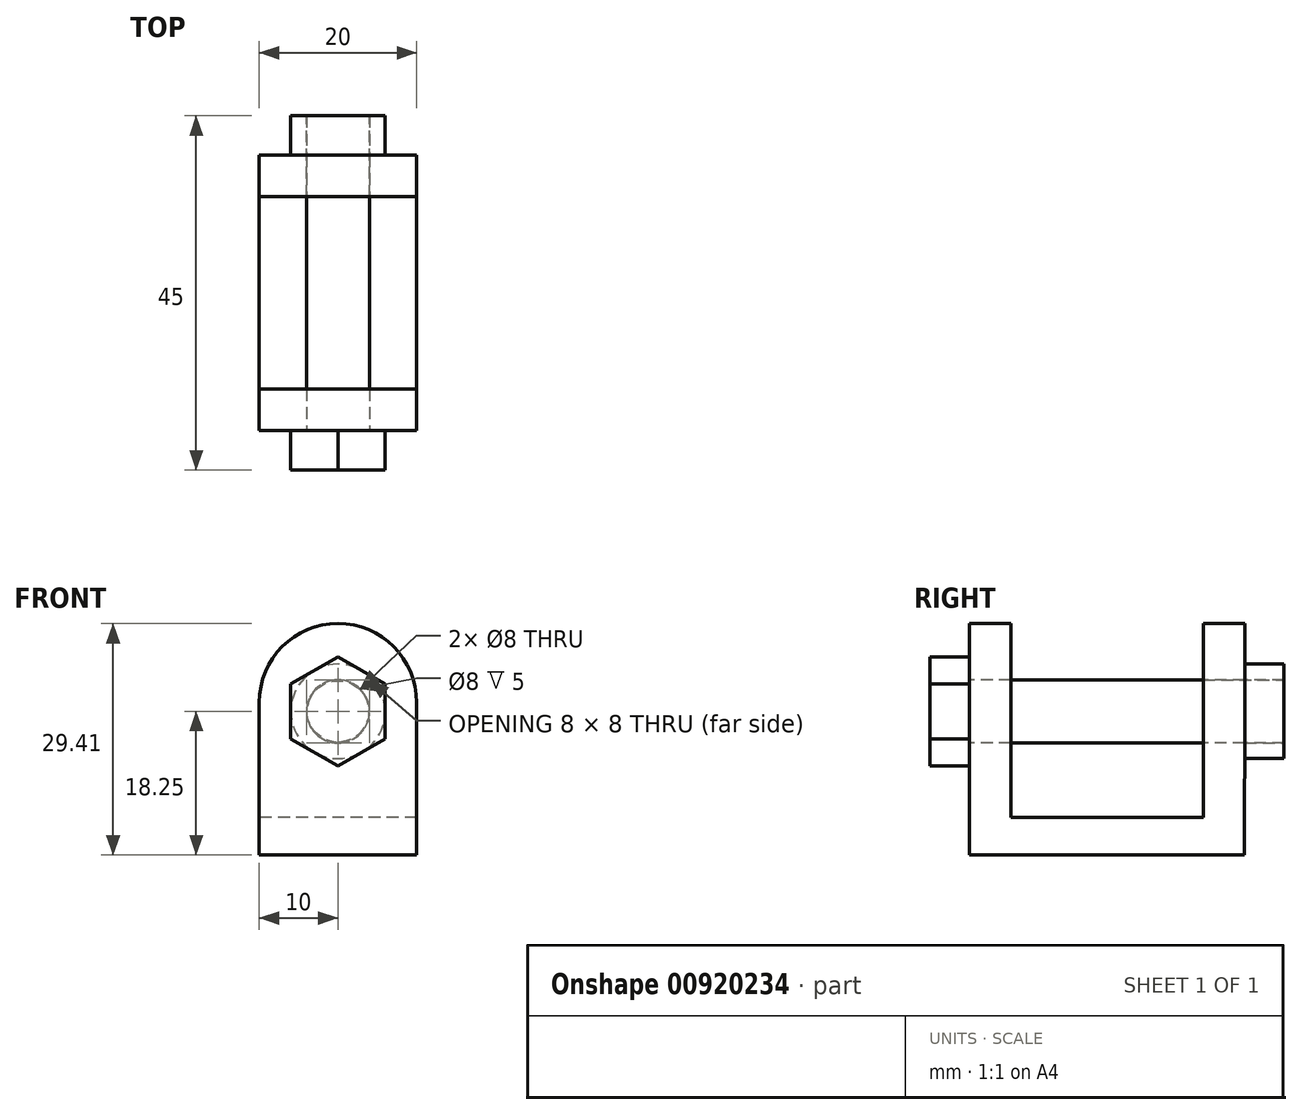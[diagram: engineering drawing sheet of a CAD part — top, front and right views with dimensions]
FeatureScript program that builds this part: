
annotation { "Feature Type Name" : "Feature", "Feature Type Description" : "" }
export const myFeature = defineFeature(function(context is Context, id is Id, definition is map)
    precondition{}
    {
        {
            var Q0;
            Q0=qCreatedBy(makeId("Front.planeOp"),FACE);
            var sketch = newSketch(context, id + "F0", { "sketchPlane" : qUnion([Q0])});
            skCircle(sketch, "E0", {"center": v(0, 0) * mm, "radius": 4 * mm});
            skSolve(sketch);
        }
        {
            var Q0;
            Q0 = qSketchRegion(id + "F0", true);
            extrude(context, id + "F1", {"entities" : qUnion([Q0]), "depth" : 40 * mm, "offsetDistance" : 25 * mm});
        }
        {
            var Q0;
            Q0=makeQuery(id+"F1.opExtrude","CAP_FACE",FACE,{"disambiguationData":[OSD([sQuery(id+"F0.wireOp",EDGE,"E0")])],"isStart":false});
            var sketch = newSketch(context, id + "F2", { "sketchPlane" : qUnion([Q0])});
            skCircle(sketch, "E1.cCircle", {"center": v(0, 0) * mm, "radius": 6 * mm, "construction": true});
            skLineSegment(sketch, "E1.0", {"start": v(6, 3.46) * mm, "end": v(6, -3.46) * mm});
            skLineSegment(sketch, "E1.1", {"start": v(6, -3.46) * mm, "end": v(0, -6.93) * mm});
            skLineSegment(sketch, "E1.2", {"start": v(0, -6.93) * mm, "end": v(-6, -3.46) * mm});
            skLineSegment(sketch, "E1.3", {"start": v(-6, -3.46) * mm, "end": v(-6, 3.46) * mm});
            skLineSegment(sketch, "E1.4", {"start": v(-6, 3.46) * mm, "end": v(0, 6.93) * mm});
            skLineSegment(sketch, "E1.5", {"start": v(0, 6.93) * mm, "end": v(6, 3.46) * mm});
            skPoint(sketch, "E1.0.midPoint", {"position": v(6, 0) * mm});
            skSolve(sketch);
        }
        {
            var Q0;
            Q0 = qSketchRegion(id + "F2", true);
            extrude(context, id + "F3", {"entities" : qUnion([Q0]), "operationType" : NewBodyOperationType.ADD, "depth" : 5 * mm, "offsetDistance" : 25 * mm});
        }
        {
            var Q0;
            Q0=makeQuery(id+"F1.opExtrude","CAP_FACE",FACE,{"disambiguationData":[OSD([sQuery(id+"F0.wireOp",EDGE,"E0")])],"isStart":true});
            var sketch = newSketch(context, id + "F4", { "sketchPlane" : qUnion([Q0])});
            skCircle(sketch, "E2", {"center": v(0, 0) * mm, "radius": 4 * mm});
            skCircle(sketch, "E3", {"center": v(0, 0) * mm, "radius": 6 * mm});
            skSolve(sketch);
        }
        {
            var Q0;
            Q0 = qSketchRegion(id + "F4", true);
            var Q1;
            Q1=makeQuery(id+"F4.imprint","IMPRINT",FACE,{"disambiguationData":[TD([[makeQuery(id+"F4.imprint","IMPRINT",EDGE,{"derivedFrom":sQuery(id+"F4.wireOp",EDGE,"E2")}),1.0]])]});
            extrude(context, id + "F5", {"entities" : qUnion([Q0, Q1]), "depth" : -5 * mm, "offsetDistance" : 25 * mm, "hasDraft" : true, "draftAngle" : 0 * degree});
        }
        {
            var Q0;
            Q0=qCreatedBy(makeId("Right.planeOp"),FACE);
            var sketch = newSketch(context, id + "F6", { "sketchPlane" : qUnion([Q0])});
            skLineSegment(sketch, "E4.top", {"start": v(-40, -18.25) * mm, "end": v(-5.02, -18.25) * mm});
            skLineSegment(sketch, "E5", {"start": v(-40, 11.16) * mm, "end": v(-40, -18.25) * mm});
            skLineSegment(sketch, "E6", {"start": v(-4.99, 11.16) * mm, "end": v(-5.02, -18.25) * mm});
            skLineSegment(sketch, "E7.right", {"start": v(-34.71, 0.02) * mm, "end": v(-34.71, 11.16) * mm});
            skLineSegment(sketch, "E8.right", {"start": v(-10.27, 0.02) * mm, "end": v(-10.27, 11.16) * mm});
            skLineSegment(sketch, "E9.top", {"start": v(-10.27, -13.48) * mm, "end": v(-34.71, -13.48) * mm});
            skLineSegment(sketch, "E9.left", {"start": v(-10.27, 0.02) * mm, "end": v(-10.27, -13.48) * mm});
            skLineSegment(sketch, "E9.right", {"start": v(-34.71, 0.02) * mm, "end": v(-34.71, -13.48) * mm});
            skLineSegment(sketch, "E10", {"start": v(-4.99, 11.16) * mm, "end": v(-10.27, 11.16) * mm});
            skLineSegment(sketch, "E11", {"start": v(-34.71, 11.16) * mm, "end": v(-40, 11.16) * mm});
            skSolve(sketch);
        }
        {
            var Q0;
            Q0 = qSketchRegion(id + "F6", true);
            extrude(context, id + "F7", {"entities" : qUnion([Q0]), "depth" : 10 * mm, "offsetDistance" : 25 * mm, "hasSecondDirection" : true, "secondDirectionOppositeDirection" : true, "secondDirectionDepth" : 10 * mm});
        }
        {
            var Q0;
            Q0=makeQuery(id+"F7.opExtrude","SWEPT_FACE",FACE,{"disambiguationData":[OSD([sQuery(id+"F6.wireOp",EDGE,"E5")])]});
            var sketch = newSketch(context, id + "F8", { "sketchPlane" : qUnion([Q0])});
            skPoint(sketch, "E12.orphan", {"position": v(10, 0) * mm});
            skPoint(sketch, "E13.top.start.orphan", {"position": v(-10, 0) * mm});
            skLineSegment(sketch, "E14.bottom", {"start": v(0, 11.16) * mm, "end": v(0, 11.16) * mm});
            skLineSegment(sketch, "E14.top", {"start": v(-10, 0) * mm, "end": v(10, 0) * mm});
            skLineSegment(sketch, "E14.left", {"start": v(-10, 1.16) * mm, "end": v(-10, 0) * mm});
            skLineSegment(sketch, "E14.right", {"start": v(10, 1.16) * mm, "end": v(10, 0) * mm});
            skPoint(sketch, "E15.visualSharp", {"position": v(-10, 11.16) * mm});
            skArc(sketch, "E15.filletArc", {"start": v(0, 11.16) * mm, "mid": v(-7.07, 8.24) * mm, "end": v(-10, 1.16) * mm});
            skPoint(sketch, "E16.visualSharp", {"position": v(10, 11.16) * mm});
            skArc(sketch, "E16.filletArc", {"start": v(10, 1.16) * mm, "mid": v(7.07, 8.24) * mm, "end": v(0, 11.16) * mm});
            skSolve(sketch);
        }
        {
            var Q0;
            {var subQ0=sQuery(id+"F8.wireOp",EDGE,"E15.filletArc");Q0=makeQuery(id+"F8.imprint","IMPRINT",FACE,{"disambiguationData":[TD([[makeQuery(id+"F8.imprint","IMPRINT",EDGE,{"derivedFrom":subQ0}),-1.0]])]});}
            var Q1;
            {var subQ0=sQuery(id+"F8.wireOp",EDGE,"E16.filletArc");Q1=makeQuery(id+"F8.imprint","IMPRINT",FACE,{"disambiguationData":[TD([[makeQuery(id+"F8.imprint","IMPRINT",EDGE,{"derivedFrom":subQ0}),-1.0]])]});}
            extrude(context, id + "F9", {"entities" : qUnion([Q0, Q1]), "depth" : -50 * mm, "offsetDistance" : 25 * mm});
        }
        {
            var Q0;
            Q0=makeQuery(id+"F9.opExtrude","SWEPT_BODY",BODY,{"disambiguationData":[OSD([sQuery(id+"F6.wireOp",EDGE,"E5"),sQuery(id+"F6.wireOp",EDGE,"E11"),sQuery(id+"F8.wireOp",EDGE,"E16.filletArc")])]});
            var Q1;
            Q1=makeQuery(id+"F7.opExtrude","SWEPT_BODY",BODY,{"disambiguationData":[OSD([sQuery(id+"F6.wireOp",EDGE,"E4.top"),sQuery(id+"F6.wireOp",EDGE,"E5"),sQuery(id+"F6.wireOp",EDGE,"E6"),sQuery(id+"F6.wireOp",EDGE,"E7.right"),sQuery(id+"F6.wireOp",EDGE,"E8.right"),sQuery(id+"F6.wireOp",EDGE,"E9.top"),sQuery(id+"F6.wireOp",EDGE,"E9.left"),sQuery(id+"F6.wireOp",EDGE,"E9.right"),sQuery(id+"F6.wireOp",EDGE,"E10"),sQuery(id+"F6.wireOp",EDGE,"E11")])]});
            booleanBodies(context, id + "F10", {"operationType" : BooleanOperationType.SUBTRACTION, "tools" : qUnion([Q0]), "targets" : qUnion([Q1])});
        }
        {
            var Q0;
            Q0=makeQuery(id+"F9.opExtrude","SWEPT_BODY",BODY,{"disambiguationData":[OSD([sQuery(id+"F6.wireOp",EDGE,"E5"),sQuery(id+"F6.wireOp",EDGE,"E11"),sQuery(id+"F8.wireOp",EDGE,"E15.filletArc")])]});
            var Q1;
            Q1=makeQuery(id+"F7.opExtrude","SWEPT_BODY",BODY,{"disambiguationData":[OSD([sQuery(id+"F6.wireOp",EDGE,"E4.top"),sQuery(id+"F6.wireOp",EDGE,"E5"),sQuery(id+"F6.wireOp",EDGE,"E6"),sQuery(id+"F6.wireOp",EDGE,"E7.right"),sQuery(id+"F6.wireOp",EDGE,"E8.right"),sQuery(id+"F6.wireOp",EDGE,"E9.top"),sQuery(id+"F6.wireOp",EDGE,"E9.left"),sQuery(id+"F6.wireOp",EDGE,"E9.right"),sQuery(id+"F6.wireOp",EDGE,"E10"),sQuery(id+"F6.wireOp",EDGE,"E11")])]});
            booleanBodies(context, id + "F11", {"operationType" : BooleanOperationType.SUBTRACTION, "tools" : qUnion([Q0]), "targets" : qUnion([Q1])});
        }
        {
            var Q0;
            Q0=makeQuery(id+"F7.opExtrude","SWEPT_FACE",FACE,{"disambiguationData":[OSD([sQuery(id+"F6.wireOp",EDGE,"E5")])]});
            var sketch = newSketch(context, id + "F12", { "sketchPlane" : qUnion([Q0])});
            skCircle(sketch, "E17", {"center": v(0, 0) * mm, "radius": 4 * mm});
            skSolve(sketch);
        }
        {
            var Q0;
            Q0 = qSketchRegion(id + "F12", true);
            extrude(context, id + "F13", {"entities" : qUnion([Q0]), "depth" : -50 * mm, "offsetDistance" : 25 * mm});
        }
        {
            var Q0;
            Q0=makeQuery(id+"F13.opExtrude","SWEPT_BODY",BODY,{"disambiguationData":[OSD([sQuery(id+"F12.wireOp",EDGE,"E17")])]});
            var Q1;
            Q1=makeQuery(id+"F7.opExtrude","SWEPT_BODY",BODY,{"disambiguationData":[OSD([sQuery(id+"F6.wireOp",EDGE,"E4.top"),sQuery(id+"F6.wireOp",EDGE,"E5"),sQuery(id+"F6.wireOp",EDGE,"E6"),sQuery(id+"F6.wireOp",EDGE,"E7.right"),sQuery(id+"F6.wireOp",EDGE,"E8.right"),sQuery(id+"F6.wireOp",EDGE,"E9.top"),sQuery(id+"F6.wireOp",EDGE,"E9.left"),sQuery(id+"F6.wireOp",EDGE,"E9.right"),sQuery(id+"F6.wireOp",EDGE,"E10"),sQuery(id+"F6.wireOp",EDGE,"E11")])]});
            booleanBodies(context, id + "F14", {"operationType" : BooleanOperationType.SUBTRACTION, "tools" : qUnion([Q0]), "targets" : qUnion([Q1])});
        }
    });
